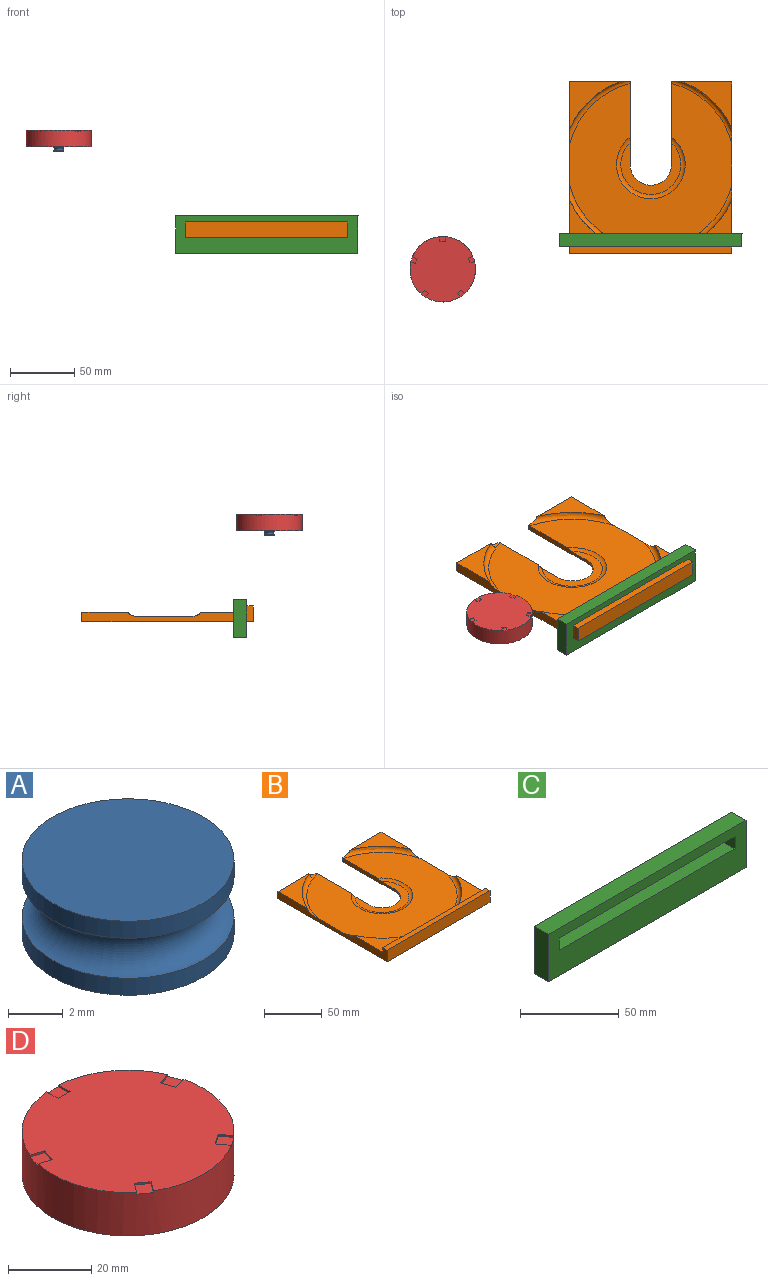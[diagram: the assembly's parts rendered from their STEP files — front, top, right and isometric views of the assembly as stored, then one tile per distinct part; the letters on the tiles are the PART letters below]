
ASSEMBLY  parts=4 mates=2
PART A: 5 faces, bbox 8.5x8.5x3.3 mm
  f0: plane 7.77x7.77mm, normal (0,0,-1), area 47.5mm2, adj f1
  f1: cylinder r=3.89mm len=7.77mm, axis (0,0,-1), area 18.6mm2, adj f0,f2
  f2: torus R=3.94mm, axis (0,0,-1), area 57.3mm2, adj f1,f3
  f3: cylinder r=3.89mm len=7.77mm, axis (0,0,-1), area 18.6mm2, adj f2,f4
  f4: plane 7.77x7.77mm, normal (0,0,1), area 47.5mm2, adj f3
PART B: 22 faces, bbox 144x145.5x12.3 mm
  f0: plane 46.76x7.62mm, normal (0,1,0), area 331.2mm2, adj f3,f5,f6,f10,f15
  f1: plane 133.06x12.31mm, normal (-1,0,0), area 842.3mm2, adj f4,f9,f10,f11,f13,f14,f17,f19
  f2: plane 37.75x36.16mm, normal (0,0,1), area 501.2mm2, adj f5,f16,f19
  f3: plane 37.75x36.16mm, normal (0,0,1), area 501.2mm2, adj f0,f5,f15
  f4: plane 37.75x36.16mm, normal (0,0,1), area 501.2mm2, adj f1,f9,f14
  f5: plane 133.06x12.31mm, normal (1,0,0), area 842.3mm2, adj f0,f2,f3,f10,f13,f15,f16,f19
  f6: plane 63.99x3.96mm, normal (-1,0,0), area 218.6mm2, adj f0,f7,f10,f12,f13,f15,f18
  f7: cylinder r=16.09mm len=32.19mm, axis (0,0,1), area 128.4mm2, adj f6,f8,f10,f12
  f8: plane 63.99x3.96mm, normal (1,0,0), area 218.6mm2, adj f7,f9,f10,f12,f13,f14,f18
  f9: plane 46.76x7.62mm, normal (0,1,0), area 331.2mm2, adj f1,f4,f8,f10,f14
  f10: plane 133.06x125.7mm, normal (0,0,-1), area 14259.4mm2, adj f0,f1,f5,f6,f7,f8,f9,f21
  f11: plane 37.75x36.16mm, normal (0,0,1), area 501.2mm2, adj f1,f17,f19
  f12: plane 46.57x40.11mm, normal (0,0,1), area 611.7mm2, adj f6,f7,f8,f18
  f13: plane 126.89x125.7mm, normal (0,0,1), area 9643.1mm2, adj f1,f5,f6,f8,f14,f15,f16,f17
  f14: torus R=64.93mm, axis (0,0,1), area 357.8mm2, adj f1,f4,f8,f9,f13
  f15: torus R=64.93mm, axis (0,0,1), area 357.7mm2, adj f0,f3,f5,f6,f13
  f16: torus R=64.93mm, axis (0,0,1), area 360.4mm2, adj f2,f5,f13,f19
  f17: torus R=64.93mm, axis (0,0,1), area 360.4mm2, adj f1,f11,f13,f19
  f18: torus R=23.28mm, axis (0,0,-1), area 449.2mm2, adj f6,f8,f12,f13
  f19: plane 125.7x8.5mm, normal (0,1,0), area 761.6mm2, adj f1,f2,f5,f11,f13,f16,f17,f20
  f20: plane 125.7x5.08mm, normal (0,0,1), area 638.6mm2, adj f1,f5,f19,f21
  f21: plane 125.7x12.31mm, normal (0,-1,0), area 1547.2mm2, adj f1,f5,f10,f20
PART C: 10 faces, bbox 141.4x10.2x29.3 mm
  f0: plane 125.72x10.16mm, normal (0,0,1), area 1277.3mm2, adj f1,f7,f8,f9
  f1: plane 10.16x7.62mm, normal (-1,0,0), area 77.4mm2, adj f0,f2,f8,f9
  f2: plane 125.72x10.16mm, normal (0,0,-1), area 1277.3mm2, adj f1,f7,f8,f9
  f3: plane 141.44x10.16mm, normal (0,0,-1), area 1437mm2, adj f4,f6,f8,f9
  f4: plane 29.32x10.16mm, normal (-1,0,0), area 297.9mm2, adj f3,f5,f8,f9
  f5: plane 141.44x10.16mm, normal (0,0,1), area 1437mm2, adj f4,f6,f8,f9
  f6: plane 29.32x10.16mm, normal (1,0,0), area 297.9mm2, adj f3,f5,f8,f9
  f7: plane 10.16x7.62mm, normal (1,0,0), area 77.4mm2, adj f0,f2,f8,f9
  f8: plane 141.44x29.32mm, normal (0,1,0), area 3189.5mm2, adj f0,f1,f2,f3,f4,f5,f6,f7
  f9: plane 141.44x29.32mm, normal (0,-1,0), area 3189.5mm2, adj f0,f1,f2,f3,f4,f5,f6,f7
PART D: 33 faces, bbox 50.8x50.8x12.7 mm
  f0: plane 50.8x50.73mm, normal (0,0,1), area 1948.3mm2, adj f2,f3,f4,f5,f7,f8,f9,f11
  f1: plane 50.8x50.8mm, normal (0,0,-1), area 1987.4mm2, adj f2,f23,f25,f27,f29,f31
  f2: cylinder r=25.4mm len=50.8mm, axis (0,0,-1), area 2016.5mm2, adj f0,f1,f3,f5,f6,f7,f9,f10
  f3: plane 3.08x2.24mm, normal (-0.81,0.59,0), area 1.9mm2, adj f0,f2,f4,f6
  f4: plane 3.28x2.38mm, normal (-0.59,-0.81,0), area 2.1mm2, adj f0,f3,f5,f6
  f5: plane 3.1x2.25mm, normal (0.81,-0.59,0), area 1.9mm2, adj f0,f2,f4,f6
  f6: plane 5.53x5.47mm, normal (0,0,1), area 15.7mm2, adj f2,f3,f4,f5
  f7: plane 3.08x2.24mm, normal (-0.81,-0.59,0), area 1.9mm2, adj f0,f2,f8,f10
  f8: plane 3.28x2.38mm, normal (0.59,-0.81,0), area 2.1mm2, adj f0,f7,f9,f10
  f9: plane 3.1x2.25mm, normal (0.81,0.59,0), area 1.9mm2, adj f0,f2,f8,f10
  f10: plane 5.52x5.49mm, normal (0,0,1), area 15.7mm2, adj f2,f7,f8,f9
  f11: plane 3.62x1.18mm, normal (0.31,-0.95,0), area 1.9mm2, adj f0,f2,f12,f14
  f12: plane 3.86x1.25mm, normal (0.95,0.31,0), area 2.1mm2, adj f0,f11,f13,f14
  f13: plane 3.65x1.19mm, normal (-0.31,0.95,0), area 1.9mm2, adj f0,f2,f12,f14
  f14: plane 5.03x4.9mm, normal (0,0,1), area 15.7mm2, adj f2,f11,f12,f13
  f15: plane 4.05x0.51mm, normal (0,1,0), area 2.1mm2, adj f0,f16,f17,f18
  f16: plane 3.84x0.51mm, normal (-1,0,0), area 1.9mm2, adj f0,f2,f15,f18
  f17: plane 3.81x0.51mm, normal (1,0,0), area 1.9mm2, adj f0,f2,f15,f18
  f18: plane 4.05x3.9mm, normal (0,0,1), area 15.7mm2, adj f2,f15,f16,f17
  f19: plane 3.62x1.18mm, normal (0.31,0.95,0), area 1.9mm2, adj f0,f2,f20,f22
  f20: plane 3.86x1.25mm, normal (-0.95,0.31,0), area 2.1mm2, adj f0,f19,f21,f22
  f21: plane 3.65x1.19mm, normal (-0.31,-0.95,0), area 1.9mm2, adj f0,f2,f20,f22
  f22: plane 5.04x4.88mm, normal (0,0,1), area 15.7mm2, adj f2,f19,f20,f21
  f23: cylinder r=1.58mm len=3.17mm, axis (0,0,-1), area 2.5mm2, adj f1,f24
  f24: plane 3.17x3.17mm, normal (0,0,-1), area 7.9mm2, adj f23
  f25: cylinder r=1.58mm len=3.17mm, axis (0,0,-1), area 2.5mm2, adj f1,f26
  f26: plane 3.17x3.17mm, normal (0,0,-1), area 7.9mm2, adj f25
  f27: cylinder r=1.58mm len=3.17mm, axis (0,0,-1), area 2.5mm2, adj f1,f28
  f28: plane 3.17x3.17mm, normal (0,0,-1), area 7.9mm2, adj f27
  f29: cylinder r=1.58mm len=3.17mm, axis (0,0,-1), area 2.5mm2, adj f1,f30
  f30: plane 3.17x3.17mm, normal (0,0,-1), area 7.9mm2, adj f29
  f31: cylinder r=1.58mm len=3.17mm, axis (0,0,-1), area 2.5mm2, adj f1,f32
  f32: plane 3.17x3.17mm, normal (0,0,-1), area 7.9mm2, adj f31
PLACE A t=(-261.97,-73.24,185.4)mm
PLACE B t=(-100.53,8.2,109.72)mm
PLACE C t=(-100.52,-119.78,113.22)mm
PLACE D rot(axis=(0.02,0.11,-0.99),0deg) t=(-261.97,-73.24,185.4)mm
MATE slider B.f21 <-> C.f8  axis (0,-1,0) through (-100.53,-60.87,108.25)mm
MATE revolute D.f2 <-> A.f1  axis (0,0,-1) through (-261.97,-73.24,172.7)mm
